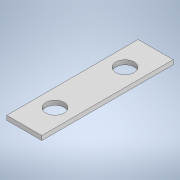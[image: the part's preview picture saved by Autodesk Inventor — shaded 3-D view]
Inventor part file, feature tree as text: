
AUTODESK INVENTOR PART (.ipt)
format: ipt  version: 2022.1 (Build 261234020, 234B)  size: 103,424 bytes
history: native  units: in
note: dims shown in document units (in); Inventor stores cm internally (conversion verified against a paired STEP export)
features: extrude x1, sketch x1
ambient origin geometry x8: Origin, YZ Plane, XZ Plane, XY Plane, X Axis, Y Axis, Z Axis, Center Point
bodies: Solid1 (feature_tree)
feature tree (2):
  extrude  "Extrusion1"  Depth=1.5in
  sketch  "Sketch1"  dims[d0=0.4in d1=1.5in d2=0.21in d3=0.21in d4=0.2in d5=0.2in d6=0.8in d7=0.35in d8=0.05in d9=0.0in]
